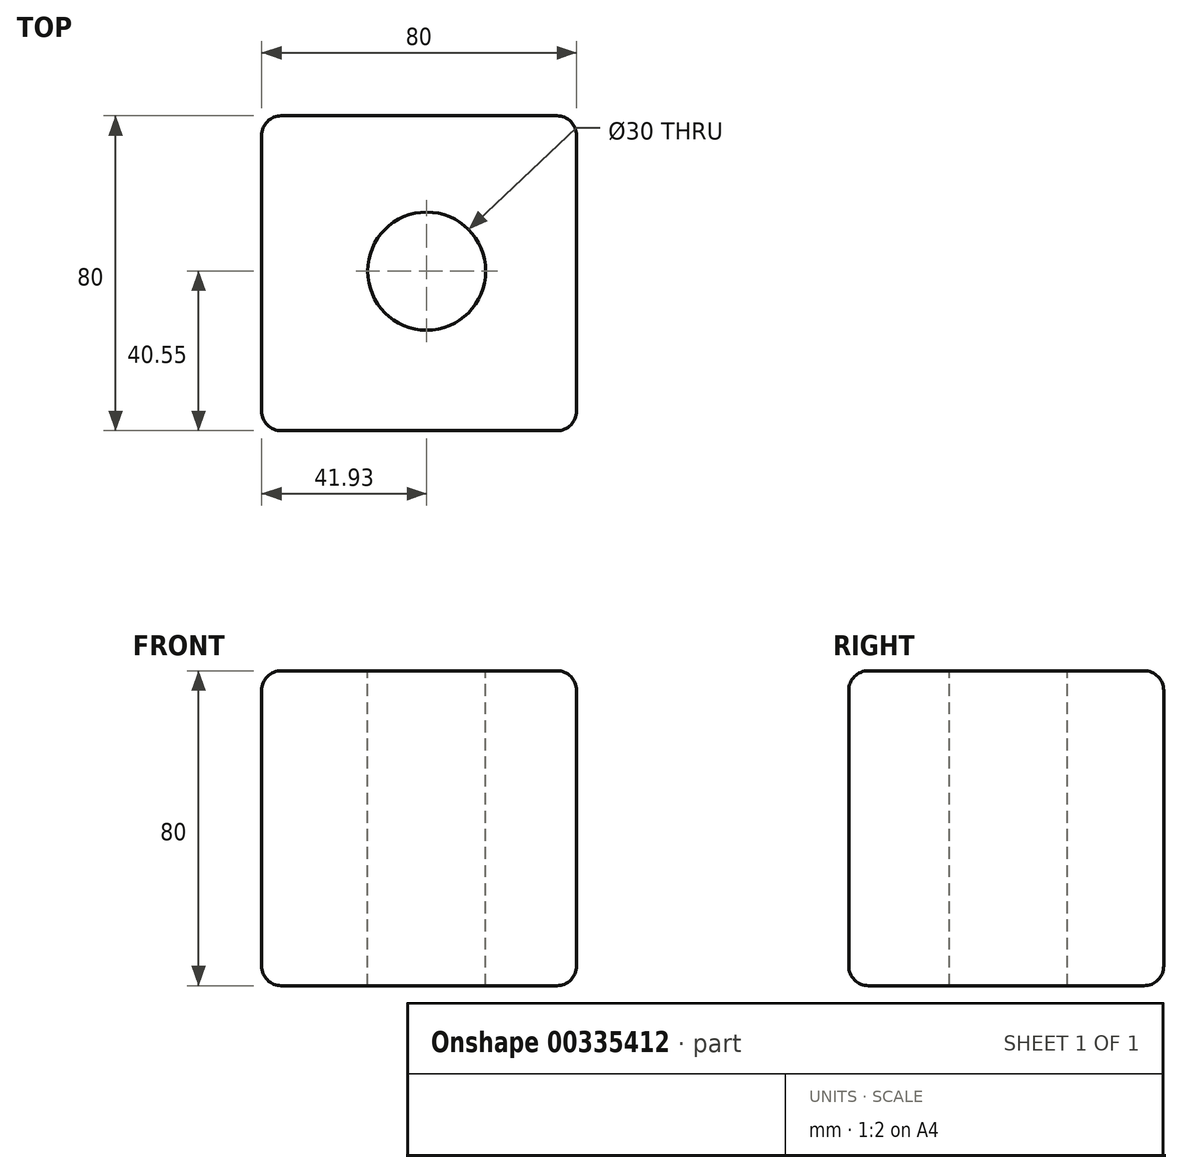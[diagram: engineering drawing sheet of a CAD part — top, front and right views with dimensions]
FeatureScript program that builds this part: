
annotation { "Feature Type Name" : "Feature", "Feature Type Description" : "" }
export const myFeature = defineFeature(function(context is Context, id is Id, definition is map)
    precondition{}
    {
        {
            var Q0;
            Q0=qCreatedBy(makeId("Top.planeOp"),FACE);
            var sketch = newSketch(context, id + "F0", { "sketchPlane" : qUnion([Q0])});
            skLineSegment(sketch, "E0.bottom", {"start": v(-41.93, 39.45) * mm, "end": v(38.07, 39.45) * mm});
            skLineSegment(sketch, "E0.top", {"start": v(-41.93, -40.55) * mm, "end": v(38.07, -40.55) * mm});
            skLineSegment(sketch, "E0.left", {"start": v(-41.93, 39.45) * mm, "end": v(-41.93, -40.55) * mm});
            skLineSegment(sketch, "E0.right", {"start": v(38.07, 39.45) * mm, "end": v(38.07, -40.55) * mm});
            skSolve(sketch);
        }
        {
            var Q0;
            Q0=makeQuery(id+"F0.imprint","IMPRINT",FACE,{"disambiguationData":[TD([[makeQuery(id+"F0.imprint","IMPRINT",EDGE,{"derivedFrom":sQuery(id+"F0.wireOp",EDGE,"E0.bottom")}),-1.0]])]});
            extrude(context, id + "F1", {"entities" : qUnion([Q0]), "endBound" : BoundingType.SYMMETRIC, "depth" : 80 * mm});
        }
        {
            var Q0;
            Q0=makeQuery(id+"F1.opExtrude","CAP_EDGE",EDGE,{"disambiguationData":[OSD([sQuery(id+"F0.wireOp",EDGE,"E0.left")])],"isStart":false});
            var Q1;
            Q1=makeQuery(id+"F1.opExtrude","CAP_EDGE",EDGE,{"disambiguationData":[OSD([sQuery(id+"F0.wireOp",EDGE,"E0.bottom")])],"isStart":false});
            var Q2;
            Q2=makeQuery(id+"F1.opExtrude","CAP_EDGE",EDGE,{"disambiguationData":[OSD([sQuery(id+"F0.wireOp",EDGE,"E0.right")])],"isStart":false});
            var Q3;
            Q3=makeQuery(id+"F1.opExtrude","CAP_EDGE",EDGE,{"disambiguationData":[OSD([sQuery(id+"F0.wireOp",EDGE,"E0.top")])],"isStart":false});
            var Q4;
            Q4=makeQuery(id+"F1.opExtrude","CAP_EDGE",EDGE,{"disambiguationData":[OSD([sQuery(id+"F0.wireOp",EDGE,"E0.top")])],"isStart":true});
            var Q5;
            Q5=makeQuery(id+"F1.opExtrude","SWEPT_EDGE",EDGE,{"disambiguationData":[OSD([sQuery(id+"F0.wireOp",EDGE,"E0.bottom"),sQuery(id+"F0.wireOp",EDGE,"E0.right")])]});
            var Q6;
            Q6=makeQuery(id+"F1.opExtrude","SWEPT_EDGE",EDGE,{"disambiguationData":[OSD([sQuery(id+"F0.wireOp",EDGE,"E0.bottom"),sQuery(id+"F0.wireOp",EDGE,"E0.left")])]});
            var Q7;
            Q7=makeQuery(id+"F1.opExtrude","CAP_EDGE",EDGE,{"disambiguationData":[OSD([sQuery(id+"F0.wireOp",EDGE,"E0.bottom")])],"isStart":true});
            var Q8;
            Q8=makeQuery(id+"F1.opExtrude","CAP_EDGE",EDGE,{"disambiguationData":[OSD([sQuery(id+"F0.wireOp",EDGE,"E0.left")])],"isStart":true});
            var Q9;
            Q9=makeQuery(id+"F1.opExtrude","SWEPT_EDGE",EDGE,{"disambiguationData":[OSD([sQuery(id+"F0.wireOp",EDGE,"E0.top"),sQuery(id+"F0.wireOp",EDGE,"E0.left")])]});
            var Q10;
            Q10=makeQuery(id+"F1.opExtrude","CAP_EDGE",EDGE,{"disambiguationData":[OSD([sQuery(id+"F0.wireOp",EDGE,"E0.right")])],"isStart":true});
            var Q11;
            Q11=makeQuery(id+"F1.opExtrude","SWEPT_EDGE",EDGE,{"disambiguationData":[OSD([sQuery(id+"F0.wireOp",EDGE,"E0.top"),sQuery(id+"F0.wireOp",EDGE,"E0.right")])]});
            fillet(context, id + "F2", {"entities" : qUnion([Q0, Q1, Q2, Q3, Q4, Q5, Q6, Q7, Q8, Q9, Q10, Q11]), "radius" : 5 * mm, "tangentPropagation" : true, "allowEdgeOverflow" : false});
        }
        {
            var Q0;
            Q0=makeQuery(id+"F1.opExtrude","CAP_FACE",FACE,{"disambiguationData":[OSD([sQuery(id+"F0.wireOp",EDGE,"E0.bottom"),sQuery(id+"F0.wireOp",EDGE,"E0.top"),sQuery(id+"F0.wireOp",EDGE,"E0.left"),sQuery(id+"F0.wireOp",EDGE,"E0.right")])],"isStart":false});
            var sketch = newSketch(context, id + "F3", { "sketchPlane" : qUnion([Q0])});
            skCircle(sketch, "E1", {"center": v(0, 0) * mm, "radius": 15 * mm});
            skSolve(sketch);
        }
        {
            var Q0;
            Q0=makeQuery(id+"F3.imprint","IMPRINT",FACE,{"disambiguationData":[TD([[makeQuery(id+"F3.imprint","IMPRINT",EDGE,{"derivedFrom":sQuery(id+"F3.wireOp",EDGE,"E1")}),1.0]])]});
            extrude(context, id + "F4", {"entities" : qUnion([Q0]), "operationType" : NewBodyOperationType.REMOVE, "endBound" : BoundingType.THROUGH_ALL, "oppositeDirection" : true, "depth" : 25 * mm});
        }
    });
